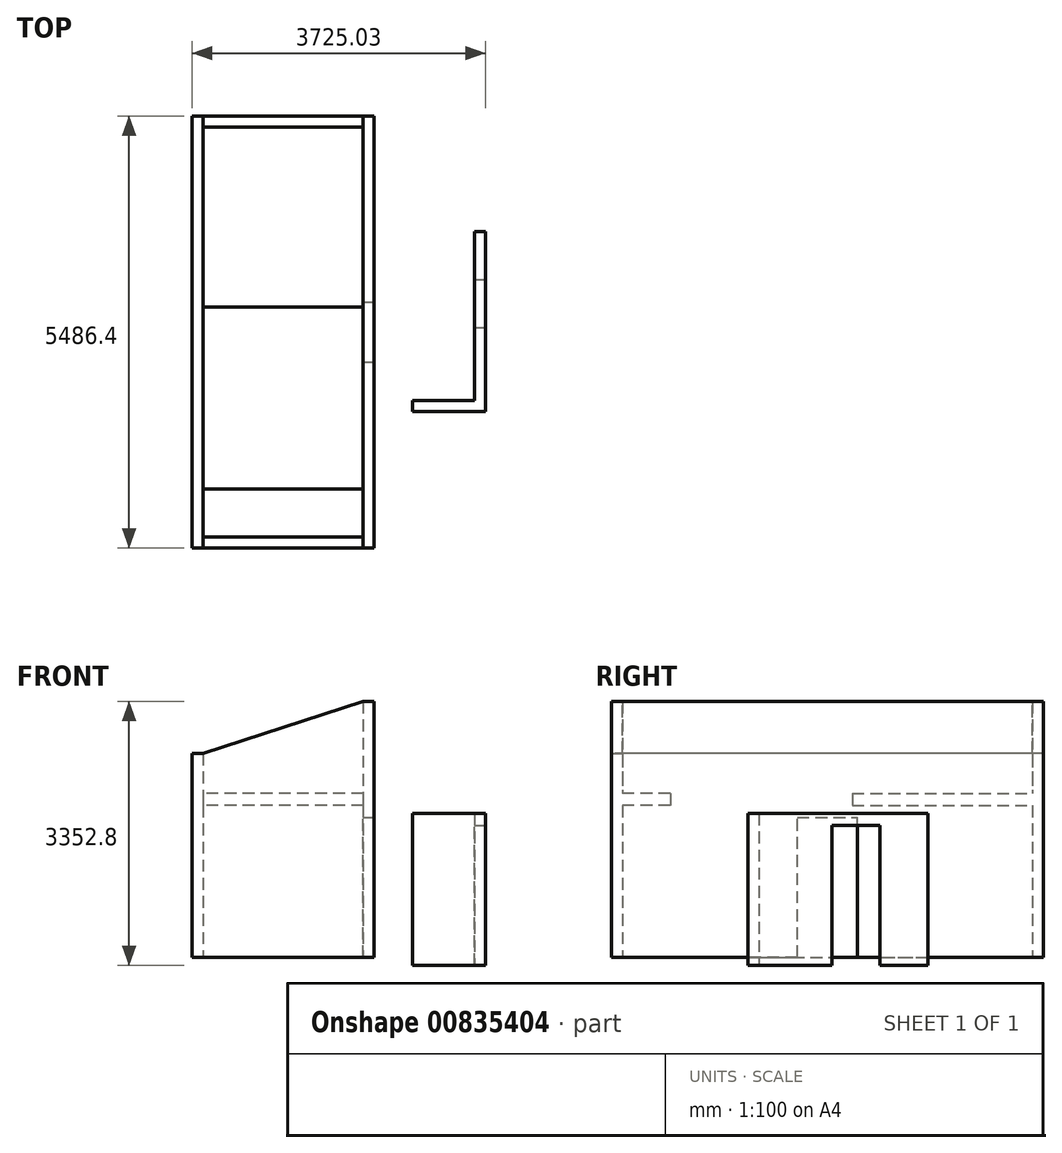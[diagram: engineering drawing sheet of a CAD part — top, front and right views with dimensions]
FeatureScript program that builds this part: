
annotation { "Feature Type Name" : "Feature", "Feature Type Description" : "" }
export const myFeature = defineFeature(function(context is Context, id is Id, definition is map)
    precondition{}
    {
        {
            var Q0;
            Q0=qCreatedBy(makeId("Top.planeOp"),FACE);
            var sketch = newSketch(context, id + "F0", { "sketchPlane" : qUnion([Q0])});
            skLineSegment(sketch, "E0.bottom", {"start": v(-1174.28, 3076.42) * mm, "end": v(1137.12, 3076.42) * mm});
            skLineSegment(sketch, "E0.top", {"start": v(-1174.28, -2409.98) * mm, "end": v(1137.12, -2409.98) * mm});
            skLineSegment(sketch, "E0.left", {"start": v(-1174.28, 3076.42) * mm, "end": v(-1174.28, -2409.98) * mm});
            skLineSegment(sketch, "E0.right", {"start": v(1137.12, 3076.42) * mm, "end": v(1137.12, -2409.98) * mm});
            skLineSegment(sketch, "E1.bottom", {"start": v(-1034.58, -2270.28) * mm, "end": v(997.42, -2270.28) * mm});
            skLineSegment(sketch, "E1.top", {"start": v(-1034.58, 2936.72) * mm, "end": v(997.42, 2936.72) * mm});
            skLineSegment(sketch, "E1.left", {"start": v(-1034.58, -2270.28) * mm, "end": v(-1034.58, 2936.72) * mm});
            skLineSegment(sketch, "E1.right", {"start": v(997.42, -2270.28) * mm, "end": v(997.42, 2936.72) * mm});
            skSolve(sketch);
        }
        {
            var Q0;
            Q0=makeQuery(id+"F0.imprint","IMPRINT",FACE,{"disambiguationData":[TD([[makeQuery(id+"F0.imprint","IMPRINT",EDGE,{"derivedFrom":sQuery(id+"F0.wireOp",EDGE,"E0.bottom")}),-1.0]])]});
            extrude(context, id + "F1", {"entities" : qUnion([Q0]), "depth" : 3352.8 * mm, "offsetDistance" : 25.4 * mm});
        }
        {
            var Q0;
            Q0=makeQuery(id+"F1.opExtrude","SWEPT_FACE",FACE,{"disambiguationData":[OSD([sQuery(id+"F0.wireOp",EDGE,"E1.top")])]});
            var sketch = newSketch(context, id + "F2", { "sketchPlane" : qUnion([Q0])});
            skLineSegment(sketch, "E2.bottom", {"start": v(997.42, 2032) * mm, "end": v(-1034.58, 2032) * mm});
            skLineSegment(sketch, "E2.top", {"start": v(997.42, 2184.4) * mm, "end": v(-1034.58, 2184.4) * mm});
            skLineSegment(sketch, "E2.left", {"start": v(997.42, 2032) * mm, "end": v(997.42, 2184.4) * mm});
            skLineSegment(sketch, "E2.right", {"start": v(-1034.58, 2032) * mm, "end": v(-1034.58, 2184.4) * mm});
            skLineSegment(sketch, "E3.bottom", {"start": v(-1034.58, 2692.4) * mm, "end": v(997.42, 2692.4) * mm});
            skLineSegment(sketch, "E3.top", {"start": v(-1034.58, 2184.4) * mm, "end": v(997.42, 2184.4) * mm});
            skLineSegment(sketch, "E3.left", {"start": v(-1034.58, 2692.4) * mm, "end": v(-1034.58, 2184.4) * mm});
            skLineSegment(sketch, "E3.right", {"start": v(997.42, 2692.4) * mm, "end": v(997.42, 2184.4) * mm});
            skLineSegment(sketch, "E4", {"start": v(-1034.58, 2692.4) * mm, "end": v(997.42, 3352.8) * mm});
            skSolve(sketch);
        }
        {
            var Q0;
            Q0=makeQuery(id+"F2.imprint","IMPRINT",FACE,{"disambiguationData":[TD([[makeQuery(id+"F2.imprint","IMPRINT",EDGE,{"derivedFrom":sQuery(id+"F2.wireOp",EDGE,"E2.bottom")}),-1.0]])]});
            extrude(context, id + "F3", {"entities" : qUnion([Q0]), "operationType" : NewBodyOperationType.ADD, "depth" : 2286 * mm, "offsetDistance" : 25.4 * mm});
        }
        {
            var Q0;
            {var subQ0=sQuery(id+"F2.wireOp",EDGE,"E4");Q0=makeQuery(id+"F2.imprint","IMPRINT",FACE,{"disambiguationData":[TD([[makeQuery(id+"F2.imprint","IMPRINT",EDGE,{"derivedFrom":subQ0}),1.0]])]});}
            extrude(context, id + "F4", {"entities" : qUnion([Q0]), "operationType" : NewBodyOperationType.REMOVE, "oppositeDirection" : true, "depth" : 139.7 * mm, "offsetDistance" : 25.4 * mm});
        }
        {
            var Q0;
            {var subQ0=sQuery(id+"F2.wireOp",EDGE,"E4");Q0=makeQuery(id+"F2.imprint","IMPRINT",FACE,{"disambiguationData":[TD([[makeQuery(id+"F2.imprint","IMPRINT",EDGE,{"derivedFrom":subQ0}),1.0]])]});}
            extrude(context, id + "F5", {"entities" : qUnion([Q0]), "operationType" : NewBodyOperationType.REMOVE, "depth" : 5473.7 * mm, "offsetDistance" : 25.4 * mm});
        }
        {
            var Q0;
            Q0=makeQuery(id+"F1.opExtrude","SWEPT_FACE",FACE,{"disambiguationData":[OSD([sQuery(id+"F0.wireOp",EDGE,"E0.top")])]});
            var sketch = newSketch(context, id + "F6", { "sketchPlane" : qUnion([Q0])});
            skLineSegment(sketch, "E5.bottom", {"start": v(-1034.58, 2692.4) * mm, "end": v(-1174.28, 2692.4) * mm});
            skLineSegment(sketch, "E5.top", {"start": v(-1034.58, 3352.8) * mm, "end": v(-1174.28, 3352.8) * mm});
            skLineSegment(sketch, "E5.left", {"start": v(-1034.58, 2692.4) * mm, "end": v(-1034.58, 3352.8) * mm});
            skLineSegment(sketch, "E5.right", {"start": v(-1174.28, 2692.4) * mm, "end": v(-1174.28, 3352.8) * mm});
            skLineSegment(sketch, "E6.bottom", {"start": v(-399.58, 0) * mm, "end": v(362.42, 0) * mm});
            skLineSegment(sketch, "E6.top", {"start": v(-399.58, 1879.6) * mm, "end": v(362.42, 1879.6) * mm});
            skLineSegment(sketch, "E6.left", {"start": v(-399.58, 0) * mm, "end": v(-399.58, 1879.6) * mm});
            skLineSegment(sketch, "E6.right", {"start": v(362.42, 0) * mm, "end": v(362.42, 1879.6) * mm});
            skSolve(sketch);
        }
        {
            var Q0;
            Q0=makeQuery(id+"F6.imprint","IMPRINT",FACE,{"disambiguationData":[TD([[makeQuery(id+"F6.imprint","IMPRINT",EDGE,{"derivedFrom":sQuery(id+"F6.wireOp",EDGE,"E5.bottom")}),-1.0]])]});
            extrude(context, id + "F7", {"entities" : qUnion([Q0]), "operationType" : NewBodyOperationType.REMOVE, "oppositeDirection" : true, "depth" : 5486.4 * mm, "offsetDistance" : 25.4 * mm});
        }
        {
            var Q0;
            Q0=makeQuery(id+"F1.opExtrude","SWEPT_FACE",FACE,{"disambiguationData":[OSD([sQuery(id+"F0.wireOp",EDGE,"E1.bottom")])]});
            var sketch = newSketch(context, id + "F8", { "sketchPlane" : qUnion([Q0])});
            skLineSegment(sketch, "E7.bottom", {"start": v(-997.42, 2032) * mm, "end": v(1034.58, 2032) * mm});
            skLineSegment(sketch, "E7.top", {"start": v(-997.42, 2184.4) * mm, "end": v(1034.58, 2184.4) * mm});
            skLineSegment(sketch, "E7.left", {"start": v(-997.42, 2032) * mm, "end": v(-997.42, 2184.4) * mm});
            skLineSegment(sketch, "E7.right", {"start": v(1034.58, 2032) * mm, "end": v(1034.58, 2184.4) * mm});
            skSolve(sketch);
        }
        {
            var Q0;
            Q0=makeQuery(id+"F8.imprint","IMPRINT",FACE,{"disambiguationData":[TD([[makeQuery(id+"F8.imprint","IMPRINT",EDGE,{"derivedFrom":sQuery(id+"F8.wireOp",EDGE,"E7.bottom")}),1.0]])]});
            extrude(context, id + "F9", {"entities" : qUnion([Q0]), "operationType" : NewBodyOperationType.ADD, "depth" : 609.6 * mm, "offsetDistance" : 25.4 * mm});
        }
        {
            var Q0;
            Q0=makeQuery(id+"F1.opExtrude","SWEPT_FACE",FACE,{"disambiguationData":[OSD([sQuery(id+"F0.wireOp",EDGE,"E0.right")])]});
            var sketch = newSketch(context, id + "F10", { "sketchPlane" : qUnion([Q0])});
            skLineSegment(sketch, "E8.bottom", {"start": v(-2409.98, 0) * mm, "end": v(3076.42, 0) * mm});
            skLineSegment(sketch, "E8.top", {"start": v(-2409.98, 101.6) * mm, "end": v(3076.42, 101.6) * mm});
            skLineSegment(sketch, "E8.left", {"start": v(-2409.98, 0) * mm, "end": v(-2409.98, 101.6) * mm});
            skLineSegment(sketch, "E8.right", {"start": v(3076.42, 0) * mm, "end": v(3076.42, 101.6) * mm});
            skSolve(sketch);
        }
        {
            var Q0;
            Q0=makeQuery(id+"F10.imprint","IMPRINT",FACE,{"disambiguationData":[TD([[makeQuery(id+"F10.imprint","IMPRINT",EDGE,{"derivedFrom":sQuery(id+"F10.wireOp",EDGE,"E8.bottom")}),-1.0]])]});
            extrude(context, id + "F11", {"entities" : qUnion([Q0]), "operationType" : NewBodyOperationType.REMOVE, "oppositeDirection" : true, "depth" : 2311.4 * mm, "offsetDistance" : 25.4 * mm});
        }
        {
            var Q0;
            Q0=qCreatedBy(makeId("Top.planeOp"),FACE);
            var sketch = newSketch(context, id + "F12", { "sketchPlane" : qUnion([Q0])});
            skLineSegment(sketch, "E9.bottom", {"start": v(1623.65, 1609.15) * mm, "end": v(2550.75, 1609.15) * mm});
            skLineSegment(sketch, "E9.top", {"start": v(1623.65, -676.85) * mm, "end": v(2550.75, -676.85) * mm});
            skLineSegment(sketch, "E9.left", {"start": v(1623.65, 1609.15) * mm, "end": v(1623.65, -676.85) * mm});
            skLineSegment(sketch, "E9.right", {"start": v(2550.75, 1609.15) * mm, "end": v(2550.75, -676.85) * mm});
            skLineSegment(sketch, "E10.bottom", {"start": v(1623.65, 1609.15) * mm, "end": v(2411.05, 1609.15) * mm});
            skLineSegment(sketch, "E10.top", {"start": v(1623.65, -537.15) * mm, "end": v(2411.05, -537.15) * mm});
            skLineSegment(sketch, "E10.left", {"start": v(1623.65, 1609.15) * mm, "end": v(1623.65, -537.15) * mm});
            skLineSegment(sketch, "E10.right", {"start": v(2411.05, 1609.15) * mm, "end": v(2411.05, -537.15) * mm});
            skSolve(sketch);
        }
        {
            var Q0;
            {var subQ2=sQuery(id+"F12.wireOp",EDGE,"E9.top");Q0=makeQuery(id+"F12.imprint","IMPRINT",FACE,{"disambiguationData":[TD([[makeQuery(id+"F12.imprint","IMPRINT",EDGE,{"derivedFrom":subQ2}),1.0]])]});}
            extrude(context, id + "F13", {"entities" : qUnion([Q0]), "depth" : 1930.4 * mm, "offsetDistance" : 25.4 * mm});
        }
        {
            var Q0;
            Q0=makeQuery(id+"F13.opExtrude","SWEPT_FACE",FACE,{"disambiguationData":[OSD([sQuery(id+"F12.wireOp",EDGE,"E9.right")])]});
            var sketch = newSketch(context, id + "F14", { "sketchPlane" : qUnion([Q0])});
            skLineSegment(sketch, "E11.bottom", {"start": v(389.95, 0) * mm, "end": v(999.55, 0) * mm});
            skLineSegment(sketch, "E11.top", {"start": v(389.95, 1778) * mm, "end": v(999.55, 1778) * mm});
            skLineSegment(sketch, "E11.left", {"start": v(389.95, 0) * mm, "end": v(389.95, 1778) * mm});
            skLineSegment(sketch, "E11.right", {"start": v(999.55, 0) * mm, "end": v(999.55, 1778) * mm});
            skSolve(sketch);
        }
        {
            var Q0;
            Q0=makeQuery(id+"F14.imprint","IMPRINT",FACE,{"disambiguationData":[TD([[makeQuery(id+"F14.imprint","IMPRINT",EDGE,{"derivedFrom":sQuery(id+"F14.wireOp",EDGE,"E11.bottom")}),-1.0]])]});
            extrude(context, id + "F15", {"entities" : qUnion([Q0]), "operationType" : NewBodyOperationType.REMOVE, "oppositeDirection" : true, "depth" : 139.7 * mm, "offsetDistance" : 25.4 * mm});
        }
        {
            var Q0;
            Q0=makeQuery(id+"F1.opExtrude","SWEPT_FACE",FACE,{"disambiguationData":[OSD([sQuery(id+"F0.wireOp",EDGE,"E0.right")])]});
            var sketch = newSketch(context, id + "F16", { "sketchPlane" : qUnion([Q0])});
            skLineSegment(sketch, "E12.bottom", {"start": v(-47.78, 101.6) * mm, "end": v(714.22, 101.6) * mm});
            skLineSegment(sketch, "E12.top", {"start": v(-47.78, 1879.6) * mm, "end": v(714.22, 1879.6) * mm});
            skLineSegment(sketch, "E12.left", {"start": v(-47.78, 101.6) * mm, "end": v(-47.78, 1879.6) * mm});
            skLineSegment(sketch, "E12.right", {"start": v(714.22, 101.6) * mm, "end": v(714.22, 1879.6) * mm});
            skSolve(sketch);
        }
        {
            var Q0;
            Q0=makeQuery(id+"F16.imprint","IMPRINT",FACE,{"disambiguationData":[TD([[makeQuery(id+"F16.imprint","IMPRINT",EDGE,{"derivedFrom":sQuery(id+"F16.wireOp",EDGE,"E12.bottom")}),1.0]])]});
            extrude(context, id + "F17", {"entities" : qUnion([Q0]), "operationType" : NewBodyOperationType.REMOVE, "oppositeDirection" : true, "depth" : 139.7 * mm, "offsetDistance" : 25.4 * mm});
        }
    });
